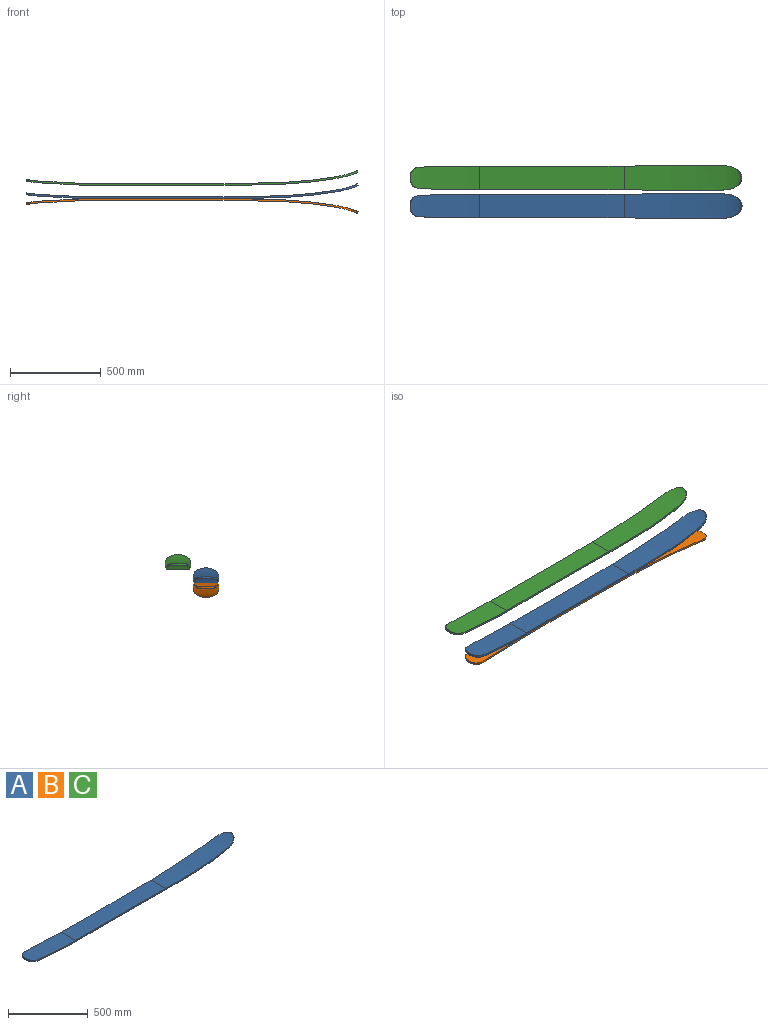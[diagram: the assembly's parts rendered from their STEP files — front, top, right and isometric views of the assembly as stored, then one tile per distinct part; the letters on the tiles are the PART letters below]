
ASSEMBLY  parts=3 mates=1
PART A: 22 faces, bbox 1830x141x81.7 mm
  f0: bspline ~110.41x34.19mm, area 1379.6mm2, adj f1,f15,f16,f19
  f1: bspline ~32.22x13.45mm, area 316.9mm2, adj f0,f2,f16,f19
  f2: bspline ~246.29x23.35mm, area 2462.3mm2, adj f1,f3,f16,f19
  f3: bspline ~72.16x10.63mm, area 720.8mm2, adj f2,f4,f16,f19
  f4: cylinder r=31791.09mm len=797.57mm, axis (0,0,1), area 7975.9mm2, adj f3,f5,f17,f20
  f5: bspline ~260.32x17.55mm, area 2602.1mm2, adj f4,f6,f18,f21
  f6: bspline ~268.71x39.37mm, area 2693.1mm2, adj f5,f7,f18,f21
  f7: bspline ~37.76x17.06mm, area 365.7mm2, adj f6,f8,f18,f21
  f8: bspline ~131.51x87.82mm, area 2404.5mm2, adj f7,f9,f18,f21
  f9: bspline ~37.76x17.06mm, area 365.7mm2, adj f8,f10,f18,f21
  f10: bspline ~268.71x39.37mm, area 2693.1mm2, adj f9,f11,f18,f21
  f11: bspline ~260.32x17.55mm, area 2602.1mm2, adj f10,f12,f18,f21
  f12: cylinder r=31791.09mm len=797.57mm, axis (0,0,1), area 7975.9mm2, adj f11,f13,f17,f20
  f13: bspline ~72.16x10.63mm, area 720.8mm2, adj f12,f14,f16,f19
  f14: bspline ~246.29x23.35mm, area 2462.3mm2, adj f13,f15,f16,f19
  f15: bspline ~32.22x13.45mm, area 316.9mm2, adj f0,f14,f16,f19
  f16: extruded ~380.91x131mm, area 47105.2mm2, adj f0,f1,f2,f3,f13,f14,f15,f17
  f17: plane 797.57x129.61mm, normal (0,0,1), area 100243mm2, adj f4,f12,f16,f18
  f18: extruded ~645.01x141mm, area 85875mm2, adj f5,f6,f7,f8,f9,f10,f11,f17
  f19: extruded ~382.43x131mm, area 47282.8mm2, adj f0,f1,f2,f3,f13,f14,f15,f20
  f20: plane 797.57x129.61mm, normal (0,0,-1), area 100243mm2, adj f4,f12,f19,f21
  f21: extruded ~650.01x141mm, area 86410.5mm2, adj f5,f6,f7,f8,f9,f10,f11,f20
PART B: same geometry as A
PART C: same geometry as A
PLACE A t=(-195.65,-385.39,164.84)mm
PLACE B rot(axis=(1,0,0),180deg) t=(-195.65,-385.39,-15.16)mm
PLACE C t=(-195.68,-230.48,238.45)mm
MATE fastened B.f20 <-> A.f20  axis (0,0,1) through (-963.81,-385.39,74.84)mm
